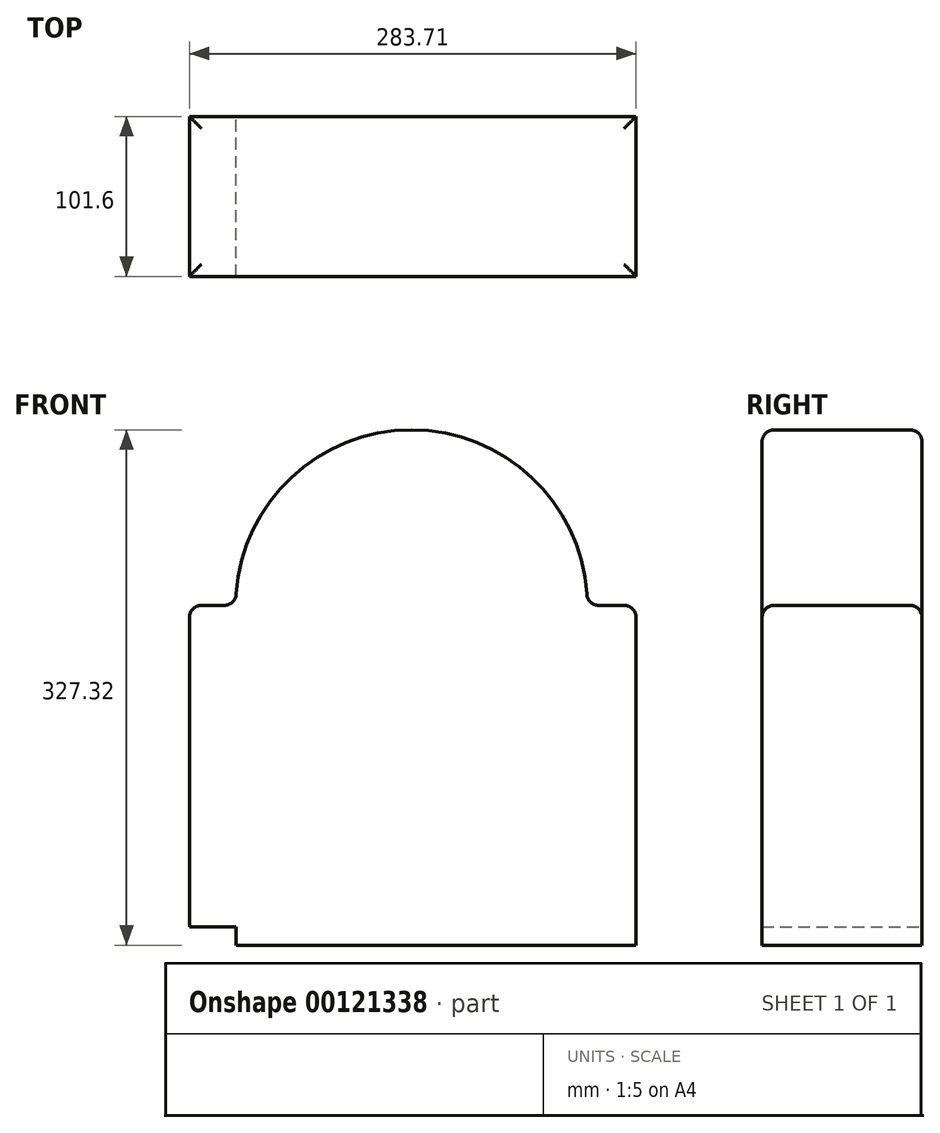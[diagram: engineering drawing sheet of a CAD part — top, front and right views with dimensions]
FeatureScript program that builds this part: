
annotation { "Feature Type Name" : "Feature", "Feature Type Description" : "" }
export const myFeature = defineFeature(function(context is Context, id is Id, definition is map)
    precondition{}
    {
        {
            var Q0;
            Q0=qCreatedBy(makeId("Front.planeOp"),FACE);
            var sketch = newSketch(context, id + "F0", { "sketchPlane" : qUnion([Q0])});
            skLineSegment(sketch, "E0.bottom", {"start": v(-111.52, 107.9) * mm, "end": v(111.52, 107.9) * mm});
            skLineSegment(sketch, "E0.top", {"start": v(-111.52, -107.9) * mm, "end": v(111.52, -107.9) * mm});
            skLineSegment(sketch, "E0.left", {"start": v(-111.52, 107.9) * mm, "end": v(-111.52, -107.9) * mm});
            skLineSegment(sketch, "E0.right", {"start": v(111.52, 107.9) * mm, "end": v(111.52, -107.9) * mm});
            skPoint(sketch, "E0.middle", {"position": v(0, 0) * mm});
            skArc(sketch, "E1", {"start": v(111.52, 107.9) * mm, "mid": v(0, 219.42) * mm, "end": v(-111.52, 107.9) * mm});
            skLineSegment(sketch, "E2", {"start": v(-111.52, 107.9) * mm, "end": v(-141.06, 107.9) * mm});
            skLineSegment(sketch, "E3", {"start": v(-141.06, 107.9) * mm, "end": v(-141.06, -96.18) * mm});
            skLineSegment(sketch, "E4", {"start": v(-141.06, -96.18) * mm, "end": v(-111.52, -96.18) * mm});
            skLineSegment(sketch, "E5", {"start": v(-111.52, -96.18) * mm, "end": v(-111.52, -96.18) * mm});
            skLineSegment(sketch, "E6", {"start": v(142.65, 107.9) * mm, "end": v(111.52, 107.9) * mm});
            skLineSegment(sketch, "E7", {"start": v(142.65, -107.9) * mm, "end": v(142.65, 107.9) * mm});
            skLineSegment(sketch, "E8", {"start": v(111.52, -107.9) * mm, "end": v(111.52, -107.9) * mm});
            skLineSegment(sketch, "E9", {"start": v(111.52, -107.9) * mm, "end": v(142.65, -107.9) * mm});
            skLineSegment(sketch, "E10", {"start": v(206.31, -37.75) * mm, "end": v(206.31, 0) * mm});
            skSolve(sketch);
        }
        {
            var Q0;
            {var subQ3=sQuery(id+"F0.wireOp",EDGE,"E0.bottom");Q0=makeQuery(id+"F0.imprint","IMPRINT",FACE,{"disambiguationData":[TD([[makeQuery(id+"F0.imprint","IMPRINT",EDGE,{"derivedFrom":subQ3}),-1.0]])]});}
            var Q1;
            Q1=makeQuery(id+"F0.imprint","IMPRINT",FACE,{"disambiguationData":[TD([[makeQuery(id+"F0.imprint","IMPRINT",EDGE,{"derivedFrom":sQuery(id+"F0.wireOp",EDGE,"E0.bottom")}),1.0]])]});
            var Q2;
            {var subQ0=sQuery(id+"F0.wireOp",EDGE,"E2");Q2=makeQuery(id+"F0.imprint","IMPRINT",FACE,{"disambiguationData":[TD([[makeQuery(id+"F0.imprint","IMPRINT",EDGE,{"derivedFrom":subQ0}),1.0]])]});}
            var Q3;
            Q3=makeQuery(id+"F0.imprint","IMPRINT",FACE,{"disambiguationData":[TD([[makeQuery(id+"F0.imprint","IMPRINT",EDGE,{"derivedFrom":sQuery(id+"F0.wireOp",EDGE,"E0.right")}),1.0]])]});
            extrude(context, id + "F1", {"entities" : qUnion([Q0, Q1, Q2, Q3]), "depth" : 101.6 * mm});
        }
        {
            var Q0;
            Q0=makeQuery(id+"F1.opExtrude","SWEPT_EDGE",EDGE,{"disambiguationData":[OSD([sQuery(id+"F0.wireOp",EDGE,"E2"),sQuery(id+"F0.wireOp",EDGE,"E3")])]});
            var Q1;
            Q1=makeQuery(id+"F1.opExtrude","CAP_EDGE",EDGE,{"disambiguationData":[OSD([sQuery(id+"F0.wireOp",EDGE,"E2")])],"isStart":true});
            var Q2;
            Q2=makeQuery(id+"F1.opExtrude","CAP_EDGE",EDGE,{"disambiguationData":[OSD([sQuery(id+"F0.wireOp",EDGE,"E2")])],"isStart":false});
            var Q3;
            Q3=makeQuery(id+"F1.opExtrude","CAP_EDGE",EDGE,{"disambiguationData":[OSD([sQuery(id+"F0.wireOp",EDGE,"E1")])],"isStart":false});
            var Q4;
            Q4=makeQuery(id+"F1.opExtrude","CAP_EDGE",EDGE,{"disambiguationData":[OSD([sQuery(id+"F0.wireOp",EDGE,"E6")])],"isStart":false});
            var Q5;
            Q5=makeQuery(id+"F1.opExtrude","SWEPT_EDGE",EDGE,{"disambiguationData":[OSD([sQuery(id+"F0.wireOp",EDGE,"E6"),sQuery(id+"F0.wireOp",EDGE,"E7")])]});
            var Q6;
            Q6=makeQuery(id+"F1.opExtrude","SWEPT_FACE",FACE,{"disambiguationData":[OSD([sQuery(id+"F0.wireOp",EDGE,"E1")])]});
            var Q7;
            Q7=makeQuery(id+"F1.opExtrude","CAP_EDGE",EDGE,{"disambiguationData":[OSD([sQuery(id+"F0.wireOp",EDGE,"E6")])],"isStart":true});
            fillet(context, id + "F2", {"entities" : qUnion([Q0, Q1, Q2, Q3, Q4, Q5, Q6, Q7]), "radius" : 7.62 * mm, "tangentPropagation" : true, "allowEdgeOverflow" : false});
        }
    });
